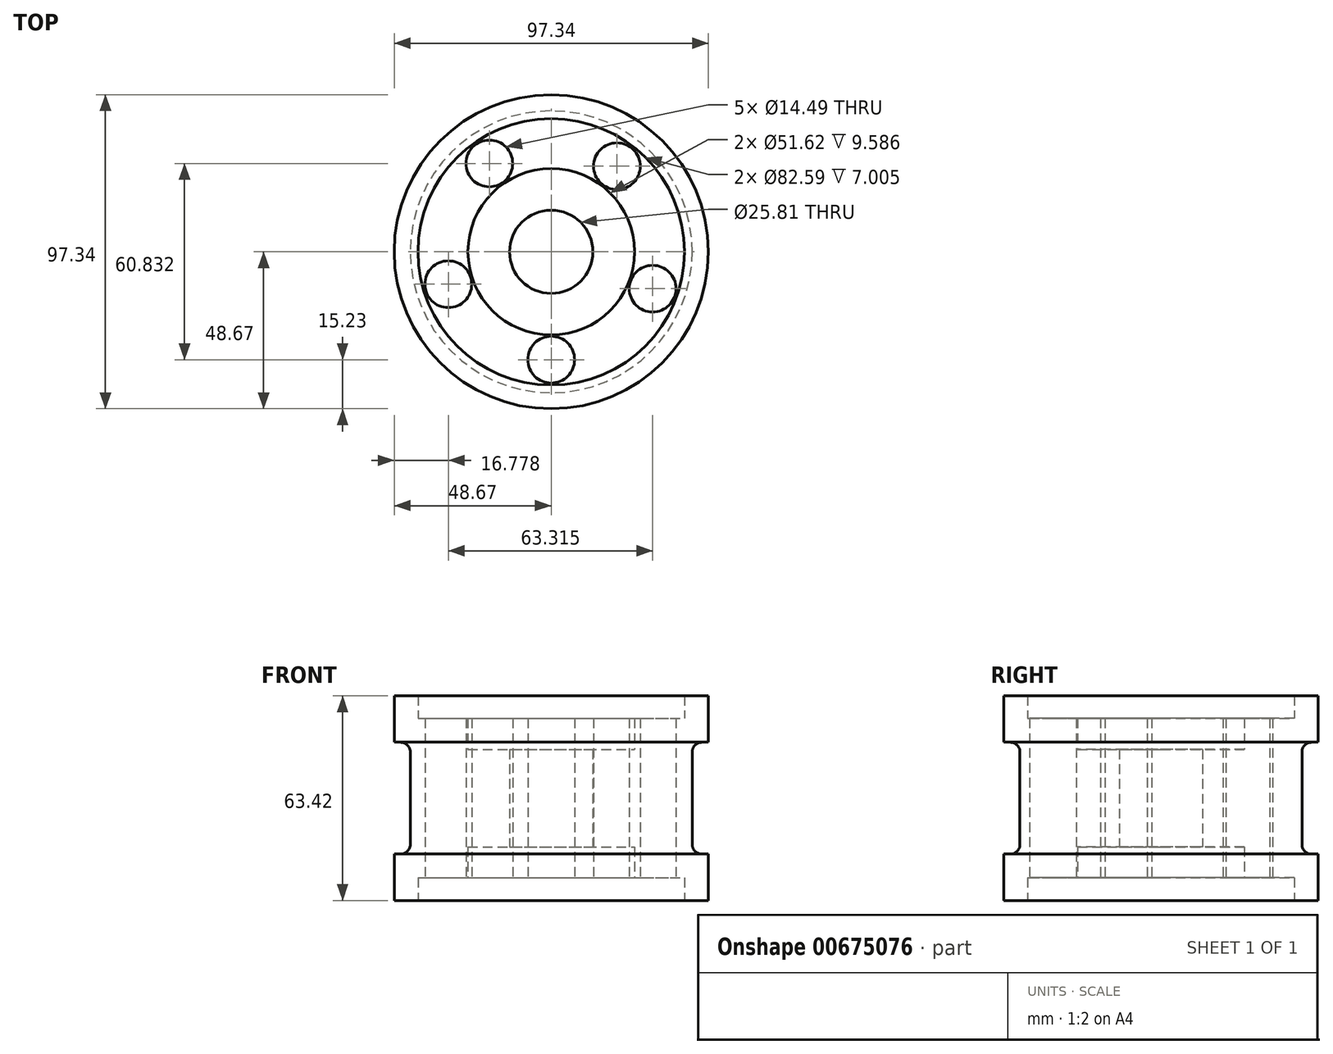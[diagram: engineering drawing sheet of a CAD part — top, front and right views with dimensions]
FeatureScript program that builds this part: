
annotation { "Feature Type Name" : "Feature", "Feature Type Description" : "" }
export const myFeature = defineFeature(function(context is Context, id is Id, definition is map)
    precondition{}
    {
        {
            var Q0;
            Q0=qCreatedBy(makeId("Front.planeOp"),FACE);
            var sketch = newSketch(context, id + "F0", { "sketchPlane" : qUnion([Q0])});
            skLineSegment(sketch, "E0", {"start": v(-55.68, 31.7) * mm, "end": v(0, 31.7) * mm, "construction": true});
            skLineSegment(sketch, "E1", {"start": v(-12.9, 31.7) * mm, "end": v(-12.9, 46.83) * mm});
            skLineSegment(sketch, "E2", {"start": v(-12.9, 46.83) * mm, "end": v(-25.8, 46.83) * mm});
            skLineSegment(sketch, "E3", {"start": v(-25.8, 46.83) * mm, "end": v(-25.8, 56.41) * mm});
            skLineSegment(sketch, "E4", {"start": v(-25.8, 56.41) * mm, "end": v(-41.3, 56.41) * mm});
            skLineSegment(sketch, "E5", {"start": v(-41.3, 56.41) * mm, "end": v(-41.3, 63.42) * mm});
            skLineSegment(sketch, "E6", {"start": v(-41.3, 63.42) * mm, "end": v(-48.67, 63.42) * mm});
            skLineSegment(sketch, "E7", {"start": v(-48.67, 63.42) * mm, "end": v(-48.67, 49.04) * mm});
            skLineSegment(sketch, "E8", {"start": v(-48.67, 49.04) * mm, "end": v(-43.7, 49.04) * mm});
            skLineSegment(sketch, "E9", {"start": v(-43.7, 49.04) * mm, "end": v(-43.7, 31.7) * mm});
            skLineSegment(sketch, "E10.MirrorCS", {"start": v(-12.9, 31.7) * mm, "end": v(-12.9, 16.6) * mm});
            skLineSegment(sketch, "E11.MirrorCS", {"start": v(-12.9, 16.6) * mm, "end": v(-25.8, 16.6) * mm});
            skLineSegment(sketch, "E12.MirrorCS", {"start": v(-41.3, 0) * mm, "end": v(-48.67, 0) * mm});
            skLineSegment(sketch, "E13.MirrorCS", {"start": v(-48.67, 0) * mm, "end": v(-48.67, 14.38) * mm});
            skLineSegment(sketch, "E14.MirrorCS", {"start": v(-25.8, 16.6) * mm, "end": v(-25.8, 7) * mm});
            skLineSegment(sketch, "E15.MirrorCS", {"start": v(-43.7, 14.38) * mm, "end": v(-43.7, 31.7) * mm});
            skLineSegment(sketch, "E16.MirrorCS", {"start": v(-25.8, 7) * mm, "end": v(-41.3, 7) * mm});
            skLineSegment(sketch, "E17.MirrorCS", {"start": v(-48.67, 14.38) * mm, "end": v(-43.7, 14.38) * mm});
            skLineSegment(sketch, "E18.MirrorCS", {"start": v(-41.3, 7) * mm, "end": v(-41.3, 0) * mm});
            skLineSegment(sketch, "E19", {"start": v(0, 31.7) * mm, "end": v(0, 72.82) * mm, "construction": true});
            skLineSegment(sketch, "E20", {"start": v(-41.3, 0) * mm, "end": v(0, 0) * mm, "construction": true});
            skSolve(sketch);
        }
        {
            var Q0;
            Q0=makeQuery(id+"F0.imprint","IMPRINT",FACE,{"disambiguationData":[TD([[makeQuery(id+"F0.imprint","IMPRINT",EDGE,{"derivedFrom":sQuery(id+"F0.wireOp",EDGE,"E1")}),1.0]])]});
            var Q1;
            Q1=sQuery(id+"F0.wireOp",EDGE,"E19");
            revolve(context, id + "F1", {"entities" : qUnion([Q0]), "axis" : qUnion([Q1]), "revolveType" : RevolveType.FULL});
        }
        {
            var Q0;
            Q0=makeQuery(id+"F1.opRevolve","SWEPT_EDGE",EDGE,{"disambiguationData":[OSD([sQuery(id+"F0.wireOp",EDGE,"E8"),sQuery(id+"F0.wireOp",EDGE,"E9")])]});
            fillet(context, id + "F2", {"entities" : qUnion([Q0]), "radius" : 3 * mm, "tangentPropagation" : true, "allowEdgeOverflow" : false});
        }
        {
            var Q0;
            Q0=makeQuery(id+"F1.opRevolve","SWEPT_EDGE",EDGE,{"disambiguationData":[OSD([sQuery(id+"F0.wireOp",EDGE,"E15.MirrorCS"),sQuery(id+"F0.wireOp",EDGE,"E17.MirrorCS")])]});
            fillet(context, id + "F3", {"entities" : qUnion([Q0]), "radius" : 3 * mm, "tangentPropagation" : true, "allowEdgeOverflow" : false});
        }
        {
            var Q0;
            Q0=qCreatedBy(makeId("Top.planeOp"),FACE);
            var sketch = newSketch(context, id + "F4", { "sketchPlane" : qUnion([Q0])});
            skCircle(sketch, "E21", {"center": v(0, 0) * mm, "radius": 40.78 * mm, "construction": true});
            skCircle(sketch, "E22", {"center": v(0, 0) * mm, "radius": 26.1 * mm, "construction": true});
            skLineSegment(sketch, "E23", {"start": v(0, -26.1) * mm, "end": v(0, -40.78) * mm, "construction": true});
            skCircle(sketch, "E24", {"center": v(0, -33.44) * mm, "radius": 7.24 * mm});
            skCircle(sketch, "E25.1.0", {"center": v(-31.9, -10.06) * mm, "radius": 7.24 * mm});
            skCircle(sketch, "E25.2.0", {"center": v(-19.18, 27.4) * mm, "radius": 7.24 * mm});
            skCircle(sketch, "E25.3.0", {"center": v(20.36, 26.53) * mm, "radius": 7.24 * mm});
            skCircle(sketch, "E25.4.0", {"center": v(31.42, -11.44) * mm, "radius": 7.24 * mm});
            skLineSegment(sketch, "E25.anchor1", {"start": v(0, 0) * mm, "end": v(0, -33.44) * mm, "construction": true});
            skLineSegment(sketch, "E25.anchor2", {"start": v(0, 0) * mm, "end": v(31.42, -11.44) * mm, "construction": true});
            skSolve(sketch);
        }
        {
            var Q0;
            Q0 = qSketchRegion(id + "F4", true);
            extrude(context, id + "F5", {"entities" : qUnion([Q0]), "operationType" : NewBodyOperationType.REMOVE, "depth" : 105.4 * mm, "offsetDistance" : 25.4 * mm});
        }
    });
